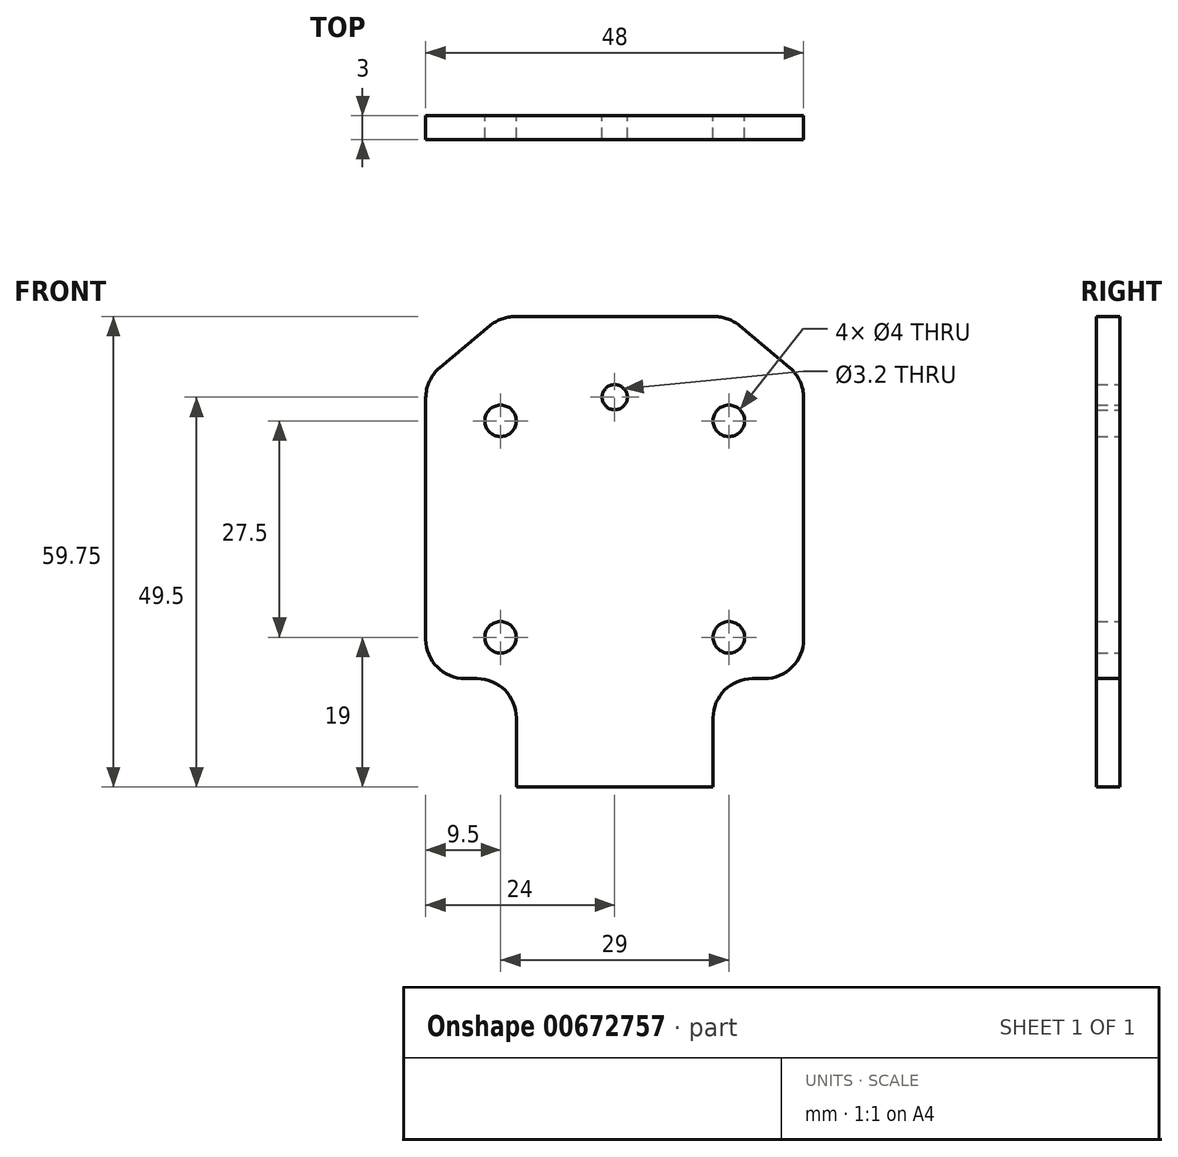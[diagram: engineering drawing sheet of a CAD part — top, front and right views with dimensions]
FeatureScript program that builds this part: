
annotation { "Feature Type Name" : "Feature", "Feature Type Description" : "" }
export const myFeature = defineFeature(function(context is Context, id is Id, definition is map)
    precondition{}
    {
        {
            var Q0;
            Q0=qCreatedBy(makeId("Front.planeOp"),FACE);
            var sketch = newSketch(context, id + "F0", { "sketchPlane" : qUnion([Q0])});
            skLineSegment(sketch, "E0.top", {"start": v(0, 38) * mm, "end": v(48, 38) * mm});
            skLineSegment(sketch, "E0.left", {"start": v(0, 5) * mm, "end": v(0, 35.67) * mm});
            skLineSegment(sketch, "E0.right", {"start": v(48, 5) * mm, "end": v(48, 35.67) * mm});
            skCircle(sketch, "E1", {"center": v(9.5, 32.75) * mm, "radius": 2 * mm});
            skCircle(sketch, "E2.1.0.0", {"center": v(38.5, 32.75) * mm, "radius": 2 * mm});
            skLineSegment(sketch, "E2.direction1", {"start": v(9.5, 32.75) * mm, "end": v(38.5, 32.75) * mm, "construction": true});
            skLineSegment(sketch, "E3.1.0.0", {"start": v(9.5, 5.25) * mm, "end": v(38.5, 5.25) * mm, "construction": true});
            skCircle(sketch, "E3.1.0.1", {"center": v(38.5, 5.25) * mm, "radius": 2 * mm});
            skCircle(sketch, "E3.1.0.2", {"center": v(9.5, 5.25) * mm, "radius": 2 * mm});
            skLineSegment(sketch, "E3.direction1", {"start": v(9.5, 32.75) * mm, "end": v(9.5, 5.25) * mm, "construction": true});
            skLineSegment(sketch, "E4", {"start": v(1.79, 39.5) * mm, "end": v(8.14, 44.83) * mm});
            skLineSegment(sketch, "E5", {"start": v(11.35, 46) * mm, "end": v(36.65, 46) * mm});
            skLineSegment(sketch, "E6", {"start": v(39.86, 44.83) * mm, "end": v(46.21, 39.5) * mm});
            skPoint(sketch, "E7.visualSharp", {"position": v(0, 38) * mm});
            skArc(sketch, "E7.filletArc", {"start": v(1.79, 39.5) * mm, "mid": v(0.47, 37.78) * mm, "end": v(0, 35.67) * mm});
            skPoint(sketch, "E8.visualSharp", {"position": v(9.53, 46) * mm});
            skArc(sketch, "E8.filletArc", {"start": v(11.35, 46) * mm, "mid": v(9.64, 45.7) * mm, "end": v(8.14, 44.83) * mm});
            skPoint(sketch, "E9.visualSharp", {"position": v(38.47, 46) * mm});
            skArc(sketch, "E9.filletArc", {"start": v(39.86, 44.83) * mm, "mid": v(38.36, 45.7) * mm, "end": v(36.65, 46) * mm});
            skPoint(sketch, "E10.visualSharp", {"position": v(48, 38) * mm});
            skArc(sketch, "E10.filletArc", {"start": v(48, 35.67) * mm, "mid": v(47.53, 37.78) * mm, "end": v(46.21, 39.5) * mm});
            skCircle(sketch, "E11", {"center": v(24, 35.75) * mm, "radius": 1.6 * mm});
            skLineSegment(sketch, "E12.top", {"start": v(11.5, -13.75) * mm, "end": v(36.5, -13.75) * mm});
            skLineSegment(sketch, "E12.left", {"start": v(11.5, -5.01) * mm, "end": v(11.5, -13.75) * mm});
            skLineSegment(sketch, "E12.right", {"start": v(36.5, -5) * mm, "end": v(36.5, -13.75) * mm});
            skLineSegment(sketch, "E13", {"start": v(5, 0) * mm, "end": v(6.5, 0) * mm});
            skLineSegment(sketch, "E14", {"start": v(11.5, -5) * mm, "end": v(11.5, -5.01) * mm});
            skLineSegment(sketch, "E15", {"start": v(36.5, -5) * mm, "end": v(36.5, -5) * mm});
            skLineSegment(sketch, "E16", {"start": v(41.5, 0) * mm, "end": v(43, 0) * mm});
            skPoint(sketch, "E17.visualSharp", {"position": v(11.5, 0) * mm});
            skArc(sketch, "E17.filletArc", {"start": v(11.5, -5) * mm, "mid": v(10.04, -1.46) * mm, "end": v(6.5, 0) * mm});
            skPoint(sketch, "E18.visualSharp", {"position": v(36.5, 0) * mm});
            skArc(sketch, "E18.filletArc", {"start": v(41.5, 0) * mm, "mid": v(37.96, -1.46) * mm, "end": v(36.5, -5) * mm});
            skPoint(sketch, "E19.visualSharp", {"position": v(0, 0) * mm});
            skArc(sketch, "E19.filletArc", {"start": v(0, 5) * mm, "mid": v(1.46, 1.46) * mm, "end": v(5, 0) * mm});
            skPoint(sketch, "E20.visualSharp", {"position": v(48, 0) * mm});
            skArc(sketch, "E20.filletArc", {"start": v(43, 0) * mm, "mid": v(46.54, 1.46) * mm, "end": v(48, 5) * mm});
            skSolve(sketch);
        }
        {
            var Q0;
            {var subQ1=sQuery(id+"F0.wireOp",EDGE,"E4");Q0=makeQuery(id+"F0.imprint","IMPRINT",FACE,{"disambiguationData":[TD([[makeQuery(id+"F0.imprint","IMPRINT",EDGE,{"derivedFrom":subQ1}),-1.0]])]});}
            var Q1;
            Q1=makeQuery(id+"F0.imprint","IMPRINT",FACE,{"disambiguationData":[TD([[makeQuery(id+"F0.imprint","IMPRINT",EDGE,{"derivedFrom":sQuery(id+"F0.wireOp",EDGE,"E0.bottom")}),1.0]])]});
            var Q2;
            {var subQ1=sQuery(id+"F0.wireOp",EDGE,"E0.left");Q2=makeQuery(id+"F0.imprint","IMPRINT",FACE,{"disambiguationData":[TD([[makeQuery(id+"F0.imprint","IMPRINT",EDGE,{"derivedFrom":subQ1}),-1.0]])]});}
            extrude(context, id + "F1", {"entities" : qUnion([Q0, Q1, Q2]), "depth" : 3 * mm, "offsetDistance" : 25 * mm});
        }
    });
